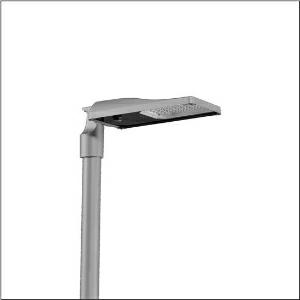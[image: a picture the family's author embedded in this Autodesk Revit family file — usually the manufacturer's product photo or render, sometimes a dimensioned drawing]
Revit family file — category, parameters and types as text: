
# Revit family: streetlight_sl_31_mini___st1_0a_5xh2d3ar08ja_7f0c
name_source: partatom
category: Lighting Fixtures
units: mm (PartAtom-declared; Revit-internal decimal feet)

## family parameters
Cut with Voids When Loaded = No
Host = Face
Light Source = No
Part Type = Normal
Room Calculation Point = No
Round Connector Dimension = Use Diameter
Shared = No

## types (1)
- --- (1 x LED, 12270 lm, 82.5 W, 3000K)
    Apparent Load = 83 VA
    CIE Flux Codes = 40 73 97 100 100
    Color Rendering = 70
    Color Temperature = 3000K
    Default Elevation = 1800 mm
    Description = Streetlight SL 31 mini D4i mast luminaire for post-top, side-entry; light control with lens of PMMA; light distribution: ST1.0a, direct asymmetric distribution, for standard-compliant lighting for roads and squares; LED: luminous flux: 12.270lm, light colour: 730, colour temperature: 3000K; luminous efficacy: 148,7lm/W; control: pre-setting: logarithmic dimming characteristic, flexible luminous flux parameterisation, time-dependent luminous flux control, constant luminous flux control, power reduction, intelligent temperature release in ECG and LED module, overheat protection; luminaire housing, of diecast aluminium, Siteco® metallic grey (DB 702S), corrosivity category C5 high according to DIN EN ISO 12944; cover of toughened safety glass, transparent, mast flange of diecast aluminium, Siteco® metallic grey (DB 702S), spigot size: 76/60mm, mast flange included unmounted; with cable H07RN-F 2x 1.5mm², cable length: 10,5m, connection cable pre-assembled; mains connection: 220..240V, AC, 50/60Hz; power consumption (at start of service life): 82,5W / (at end of service life): 90,1W / (with reduced operation 50%): 36,8W; protection rating (complete): IP66; insulation class (complete): insulation class II (safety insulation); impact resistance: IK09; certification: CE, ENEC, ENEC+, VDE, UKCA, ZD4i; permissible operating ambient temperature for outdoor applications: -40..+50°C; packaging unit: 1 piece

Light Distribution: ST1.0a
    Height = 76 mm
    Lamp = 1 x LED
    Lamp Light Flux = 12270 lm
    Lamp Power = 82.5 W
    Lamp count = 1
    Length = 547 mm
    Luminous efficacy = 149 lm/W
    Manufacturer = Siteco
    ModVariant = No
    Model = 5XH2D3AR08JA
    Number of Poles = 1
    OnlyDefault = Yes
    Power Factor = 1
    Product Name = Streetlight SL 31 mini | ST1.0a
    Product group = mast luminaire | pylon top
    ProductGroupID = 6100
    Protection Class = Protection class II
    Protection Degree = IP 66
    RLX_Detail_Level = 1
    RLX_Emergency_Light_Flux = 0 lm
    RLX_Emergency_Type = 0
    RLX_Emergency_Type_DB = No
    RlxData = <blob elided: 39761 chars, md5=23cb433d>
    Socket = socket
    Standby Power = 0 W
    System Light Flux = 12270 lm
    System Power = 83 W
    Type Comments = factory setting: luminous flux: 100 % | dim-lin: 254 | 870 mA
    Type Image = l_1300328.jpg
    URL = http://relux.com
    VarID = @adj_050926
    Voltage = 0 V
    Weight = 0.00 kg
    Width = 265 mm

## geometry (parser evidence)
native form markers: Blend x4, Sweep x9
no freeform markers — native parametric forms only
